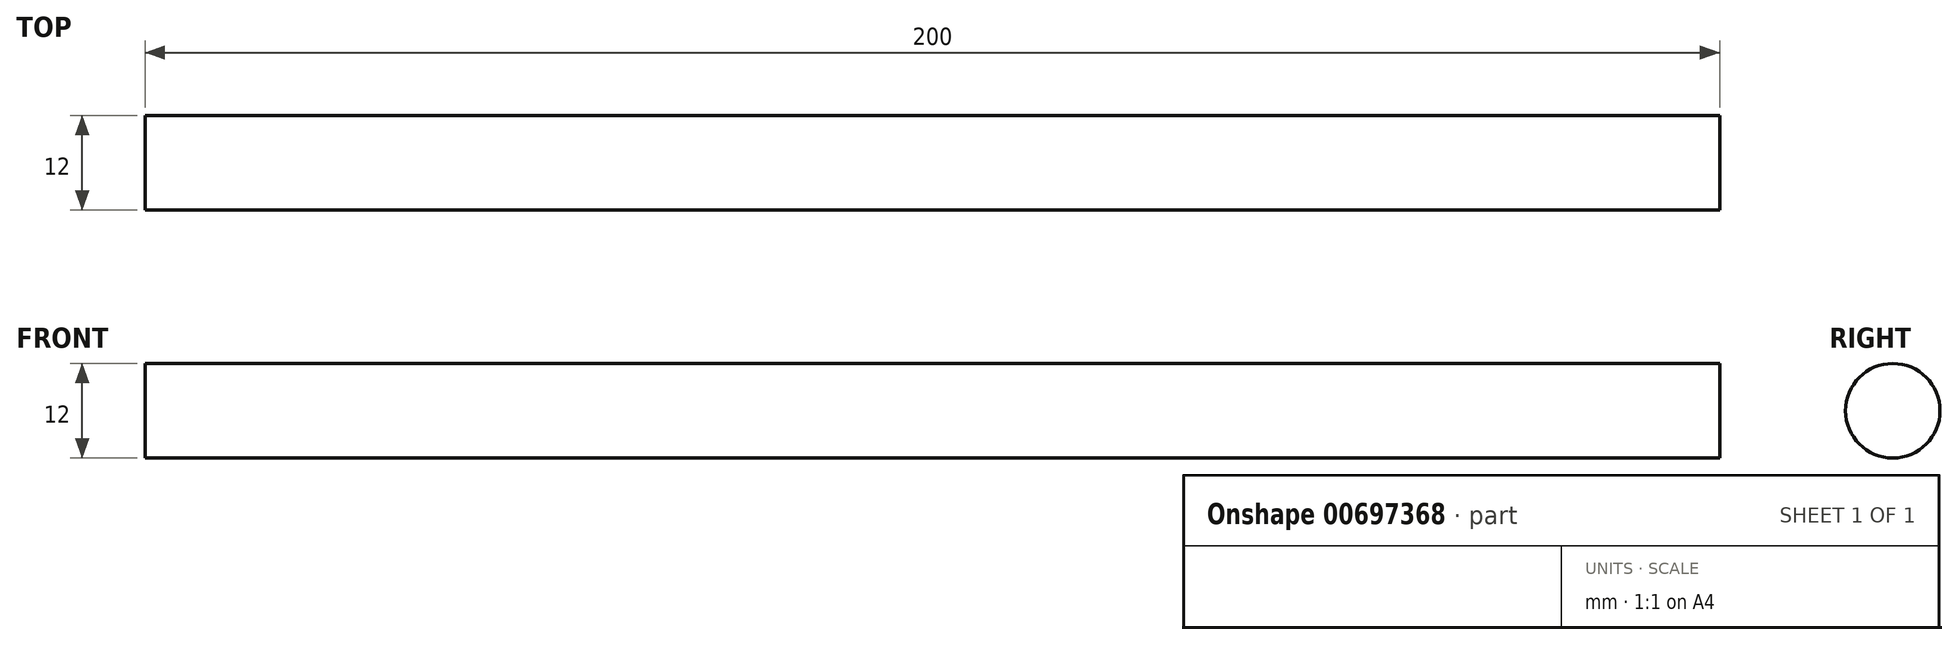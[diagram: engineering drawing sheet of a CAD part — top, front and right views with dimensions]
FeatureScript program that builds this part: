
annotation { "Feature Type Name" : "Feature", "Feature Type Description" : "" }
export const myFeature = defineFeature(function(context is Context, id is Id, definition is map)
    precondition{}
    {
        {
            var Q0;
            Q0=qCreatedBy(makeId("Right.planeOp"),FACE);
            var sketch = newSketch(context, id + "F0", { "sketchPlane" : qUnion([Q0])});
            skCircle(sketch, "E0", {"center": v(0, 0) * mm, "radius": 6 * mm});
            skSolve(sketch);
        }
        {
            var Q0;
            Q0=makeQuery(id+"F0.imprint","IMPRINT",FACE,{"disambiguationData":[TD([[makeQuery(id+"F0.imprint","IMPRINT",EDGE,{"derivedFrom":sQuery(id+"F0.wireOp",EDGE,"E0")}),1.0]])]});
            extrude(context, id + "F1", {"entities" : qUnion([Q0]), "depth" : 200 * mm, "offsetDistance" : 25 * mm});
        }
    });
